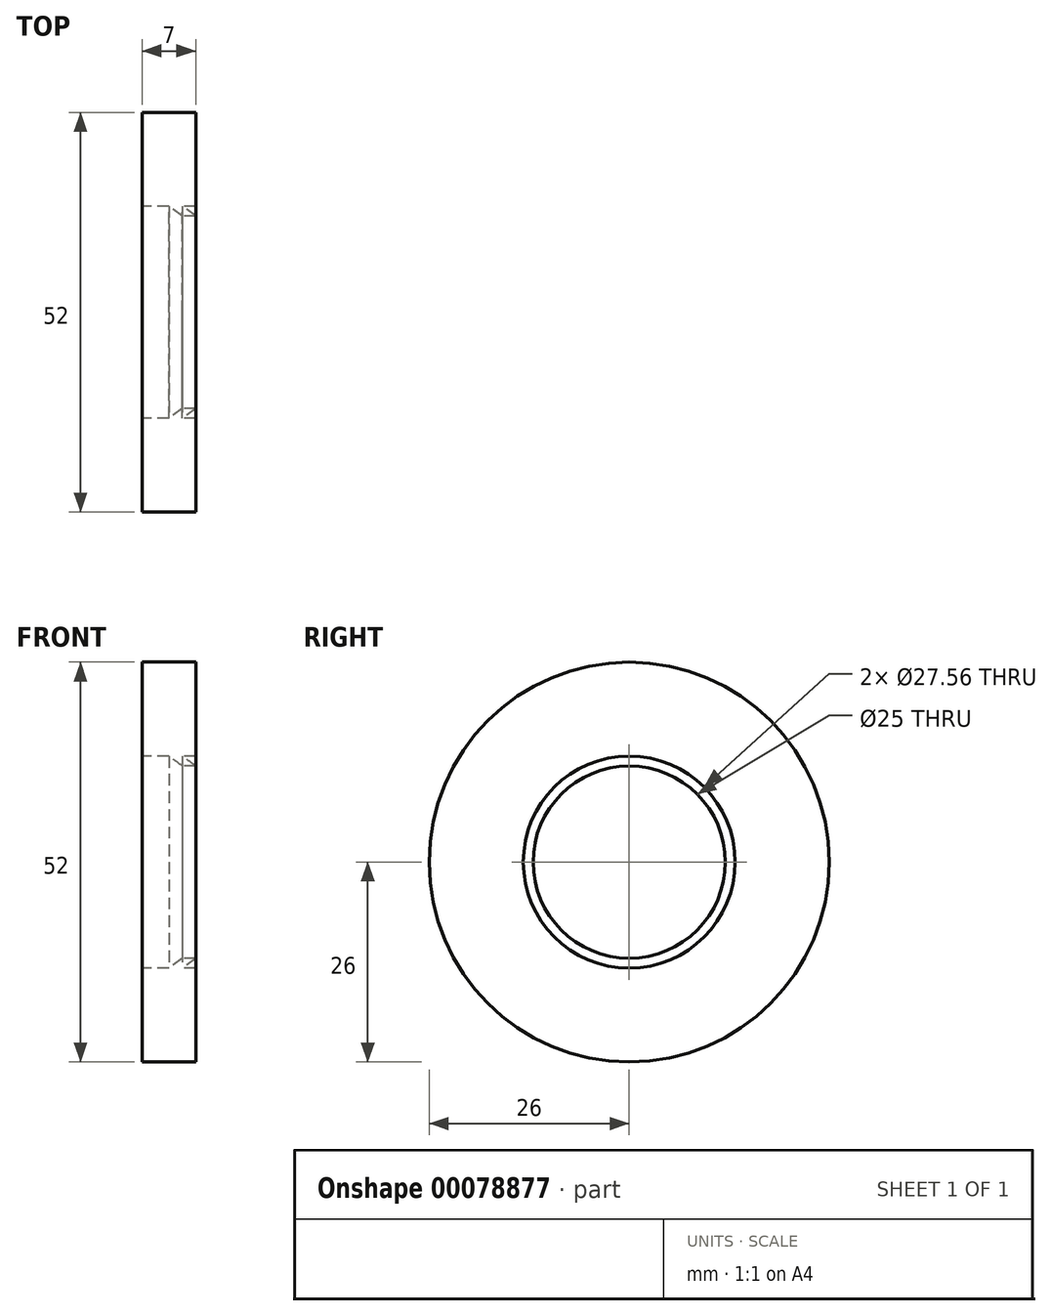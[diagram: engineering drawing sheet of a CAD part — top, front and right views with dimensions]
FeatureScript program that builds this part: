
annotation { "Feature Type Name" : "Feature", "Feature Type Description" : "" }
export const myFeature = defineFeature(function(context is Context, id is Id, definition is map)
    precondition{}
    {
        {
            var Q0;
            Q0=qCreatedBy(makeId("Front.planeOp"),FACE);
            var sketch = newSketch(context, id + "F0", { "sketchPlane" : qUnion([Q0])});
            skLineSegment(sketch, "E0.bottom", {"start": v(0, 26) * mm, "end": v(7, 26) * mm});
            skLineSegment(sketch, "E0.top", {"start": v(5.25, 12.5) * mm, "end": v(7, 12.5) * mm});
            skLineSegment(sketch, "E0.left", {"start": v(0, 26) * mm, "end": v(0, 13.78) * mm});
            skLineSegment(sketch, "E0.right", {"start": v(7, 26) * mm, "end": v(7, 13.78) * mm});
            skLineSegment(sketch, "E1", {"start": v(0, 13.78) * mm, "end": v(3.5, 13.78) * mm});
            skLineSegment(sketch, "E2", {"start": v(3.5, 13.78) * mm, "end": v(5.25, 12.5) * mm});
            skLineSegment(sketch, "E3", {"start": v(7, 12.5) * mm, "end": v(5.25, 13.78) * mm});
            skLineSegment(sketch, "E4", {"start": v(5.25, 13.78) * mm, "end": v(7, 13.78) * mm});
            skLineSegment(sketch, "E5", {"start": v(3.5, 26) * mm, "end": v(3.5, 9.73) * mm, "construction": true});
            skLineSegment(sketch, "E6", {"start": v(3.5, 13.78) * mm, "end": v(7, 13.78) * mm, "construction": true});
            skLineSegment(sketch, "E7", {"start": v(5.25, 13.78) * mm, "end": v(5.25, 11.77) * mm, "construction": true});
            skLineSegment(sketch, "E8", {"start": v(0, 0) * mm, "end": v(15, 0) * mm, "construction": true});
            skSolve(sketch);
        }
        {
            var Q0;
            Q0=makeQuery(id+"F0.imprint","IMPRINT",FACE,{"disambiguationData":[TD([[makeQuery(id+"F0.imprint","IMPRINT",EDGE,{"derivedFrom":sQuery(id+"F0.wireOp",EDGE,"E0.bottom")}),-1.0]])]});
            var Q1;
            Q1=sQuery(id+"F0.wireOp",EDGE,"E8");
            revolve(context, id + "F1", {"entities" : qUnion([Q0]), "axis" : qUnion([Q1]), "revolveType" : RevolveType.FULL});
        }
    });
